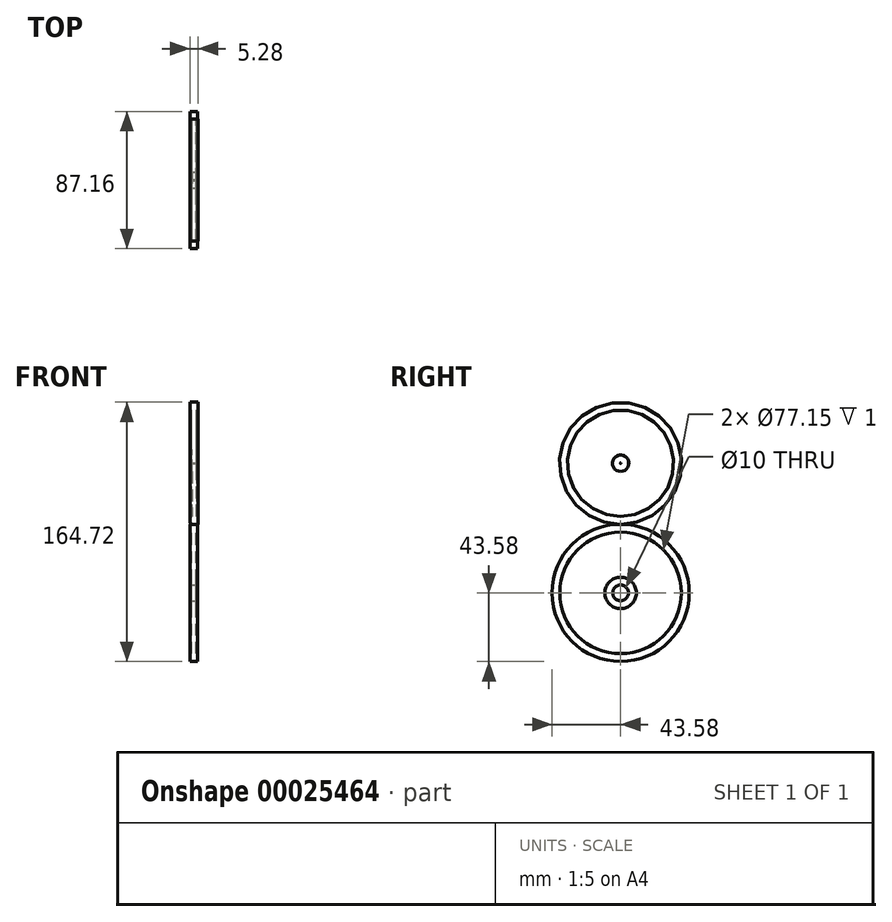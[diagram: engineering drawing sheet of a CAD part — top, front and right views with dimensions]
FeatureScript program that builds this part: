
annotation { "Feature Type Name" : "Feature", "Feature Type Description" : "" }
export const myFeature = defineFeature(function(context is Context, id is Id, definition is map)
    precondition{}
    {
        {
            var Q0;
            Q0=qCreatedBy(makeId("Front.planeOp"),FACE);
            var sketch = newSketch(context, id + "F0", { "sketchPlane" : qUnion([Q0])});
            skLineSegment(sketch, "E0", {"start": v(0, 0) * mm, "end": v(-139.16, 0) * mm, "construction": true});
            skLineSegment(sketch, "E1.left", {"start": v(-33.09, 38.58) * mm, "end": v(-33.09, 10) * mm});
            skLineSegment(sketch, "E1.right", {"start": v(-30.09, 38.58) * mm, "end": v(-30.09, 10) * mm});
            skLineSegment(sketch, "E2.top", {"start": v(-34.09, 5) * mm, "end": v(-29.09, 5) * mm});
            skLineSegment(sketch, "E2.left", {"start": v(-34.09, 10) * mm, "end": v(-34.09, 5) * mm});
            skLineSegment(sketch, "E2.right", {"start": v(-29.09, 10) * mm, "end": v(-29.09, 5) * mm});
            skLineSegment(sketch, "E3.bottom", {"start": v(-34.09, 43.58) * mm, "end": v(-29.09, 43.58) * mm});
            skLineSegment(sketch, "E3.left", {"start": v(-34.09, 43.58) * mm, "end": v(-34.09, 38.58) * mm});
            skLineSegment(sketch, "E3.right", {"start": v(-29.09, 43.58) * mm, "end": v(-29.09, 38.57) * mm});
            skLineSegment(sketch, "E2.bottom", {"start": v(-34.09, 10) * mm, "end": v(-29.09, 10) * mm});
            skLineSegment(sketch, "E1.top", {"start": v(-33.09, 10) * mm, "end": v(-30.09, 10) * mm});
            skLineSegment(sketch, "E3.top", {"start": v(-34.09, 38.58) * mm, "end": v(-29.09, 38.58) * mm});
            skLineSegment(sketch, "E1.bottom", {"start": v(-33.09, 38.58) * mm, "end": v(-30.09, 38.58) * mm});
            skLineSegment(sketch, "E4", {"start": v(-33.09, 38.58) * mm, "end": v(-30.09, 38.58) * mm, "construction": true});
            skLineSegment(sketch, "E5", {"start": v(-31.3, 0) * mm, "end": v(-31.3, 91.93) * mm, "construction": true});
            skLineSegment(sketch, "E6.left", {"start": v(-32.8, 77.15) * mm, "end": v(-32.8, 48.58) * mm});
            skLineSegment(sketch, "E6.right", {"start": v(-29.8, 77.15) * mm, "end": v(-29.8, 48.58) * mm});
            skLineSegment(sketch, "E7.top", {"start": v(-33.8, 43.58) * mm, "end": v(-28.8, 43.58) * mm});
            skLineSegment(sketch, "E7.left", {"start": v(-33.8, 48.58) * mm, "end": v(-33.8, 43.58) * mm});
            skLineSegment(sketch, "E7.right", {"start": v(-28.8, 48.58) * mm, "end": v(-28.8, 43.58) * mm});
            skLineSegment(sketch, "E8.bottom", {"start": v(-33.8, 82.15) * mm, "end": v(-28.8, 82.15) * mm});
            skLineSegment(sketch, "E8.left", {"start": v(-33.8, 82.15) * mm, "end": v(-33.8, 77.15) * mm});
            skLineSegment(sketch, "E8.right", {"start": v(-28.8, 82.15) * mm, "end": v(-28.8, 77.15) * mm});
            skLineSegment(sketch, "E7.bottom", {"start": v(-33.8, 48.58) * mm, "end": v(-28.8, 48.58) * mm});
            skLineSegment(sketch, "E6.top", {"start": v(-32.8, 48.58) * mm, "end": v(-29.8, 48.58) * mm});
            skLineSegment(sketch, "E8.top", {"start": v(-33.8, 77.15) * mm, "end": v(-28.8, 77.15) * mm});
            skLineSegment(sketch, "E6.bottom", {"start": v(-32.8, 77.15) * mm, "end": v(-29.8, 77.15) * mm});
            skLineSegment(sketch, "E9", {"start": v(-32.8, 77.15) * mm, "end": v(-29.8, 77.15) * mm, "construction": true});
            skLineSegment(sketch, "E10", {"start": v(18.78, 82.47) * mm, "end": v(-115.38, 82.15) * mm, "construction": true});
            skSolve(sketch);
        }
        {
            var Q0;
            Q0=makeQuery(id+"F0.imprint","IMPRINT",FACE,{"disambiguationData":[TD([[makeQuery(id+"F0.imprint","IMPRINT",EDGE,{"derivedFrom":sQuery(id+"F0.wireOp",EDGE,"E2.top")}),1.0]])]});
            var Q1;
            Q1=makeQuery(id+"F0.imprint","IMPRINT",FACE,{"disambiguationData":[TD([[makeQuery(id+"F0.imprint","IMPRINT",EDGE,{"derivedFrom":sQuery(id+"F0.wireOp",EDGE,"E1.left")}),1.0]])]});
            var Q2;
            {var subQ2=sQuery(id+"F0.wireOp",EDGE,"E3.bottom");Q2=makeQuery(id+"F0.imprint","IMPRINT",FACE,{"disambiguationData":[TD([[makeQuery(id+"F0.imprint","IMPRINT",EDGE,{"derivedFrom":subQ2}),-1.0]])]});}
            var Q3;
            Q3=sQuery(id+"F0.wireOp",EDGE,"E0");
            revolve(context, id + "F1", {"entities" : qUnion([Q0, Q1, Q2]), "axis" : qUnion([Q3]), "revolveType" : RevolveType.FULL});
        }
        {
            var Q0;
            {var subQ3=sQuery(id+"F0.wireOp",EDGE,"E7.left");Q0=makeQuery(id+"F0.imprint","IMPRINT",FACE,{"disambiguationData":[TD([[makeQuery(id+"F0.imprint","IMPRINT",EDGE,{"derivedFrom":subQ3}),1.0]])]});}
            var Q1;
            Q1=makeQuery(id+"F0.imprint","IMPRINT",FACE,{"disambiguationData":[TD([[makeQuery(id+"F0.imprint","IMPRINT",EDGE,{"derivedFrom":sQuery(id+"F0.wireOp",EDGE,"E6.left")}),1.0]])]});
            var Q2;
            Q2=makeQuery(id+"F0.imprint","IMPRINT",FACE,{"disambiguationData":[TD([[makeQuery(id+"F0.imprint","IMPRINT",EDGE,{"derivedFrom":sQuery(id+"F0.wireOp",EDGE,"E8.bottom")}),-1.0]])]});
            var Q3;
            Q3=sQuery(id+"F0.wireOp",EDGE,"E10");
            revolve(context, id + "F2", {"operationType" : NewBodyOperationType.ADD, "entities" : qUnion([Q0, Q1, Q2]), "axis" : qUnion([Q3]), "revolveType" : RevolveType.FULL});
        }
    });
